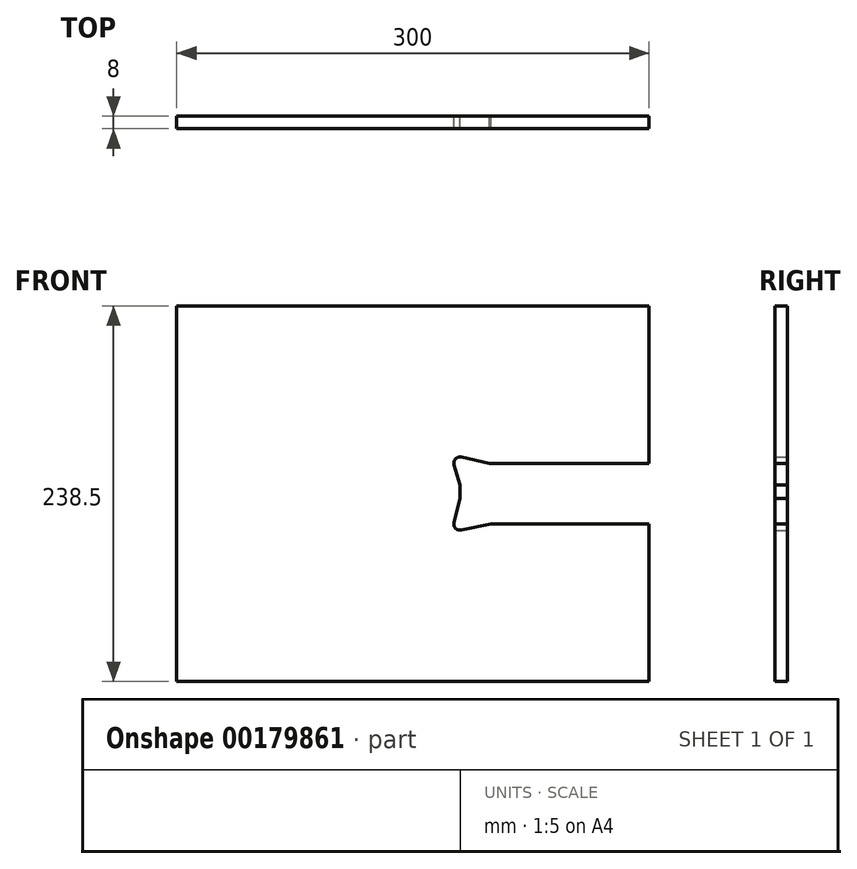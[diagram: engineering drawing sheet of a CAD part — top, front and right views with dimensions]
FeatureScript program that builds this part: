
annotation { "Feature Type Name" : "Feature", "Feature Type Description" : "" }
export const myFeature = defineFeature(function(context is Context, id is Id, definition is map)
    precondition{}
    {
        {
            var Q0;
            Q0=qCreatedBy(makeId("Front.planeOp"),FACE);
            var sketch = newSketch(context, id + "F0", { "sketchPlane" : qUnion([Q0])});
            skLineSegment(sketch, "E0", {"start": v(-40.97, 135.67) * mm, "end": v(79.03, 135.67) * mm});
            skLineSegment(sketch, "E1", {"start": v(79.03, 135.67) * mm, "end": v(79.03, 235.67) * mm});
            skLineSegment(sketch, "E2", {"start": v(79.03, 235.67) * mm, "end": v(-220.97, 235.67) * mm});
            skLineSegment(sketch, "E3", {"start": v(-40.97, 97.17) * mm, "end": v(-40.97, 135.67) * mm});
            skLineSegment(sketch, "E4", {"start": v(-40.97, 97.17) * mm, "end": v(79.03, 97.17) * mm});
            skLineSegment(sketch, "E5", {"start": v(79.03, 97.17) * mm, "end": v(79.03, -2.83) * mm});
            skLineSegment(sketch, "E6", {"start": v(79.03, -2.83) * mm, "end": v(-220.97, -2.83) * mm});
            skLineSegment(sketch, "E7", {"start": v(-220.97, -2.83) * mm, "end": v(-220.97, 235.67) * mm});
            skCircle(sketch, "E8", {"center": v(-40.97, 135.67) * mm, "radius": 4 * mm});
            skCircle(sketch, "E9", {"center": v(-40.97, 97.17) * mm, "radius": 4 * mm});
            skLineSegment(sketch, "E10", {"start": v(-40.11, 139.58) * mm, "end": v(-22.22, 135.67) * mm});
            skLineSegment(sketch, "E11", {"start": v(-44.8, 134.51) * mm, "end": v(-40.97, 121.87) * mm});
            skLineSegment(sketch, "E12", {"start": v(-44.84, 98.17) * mm, "end": v(-40.97, 113.2) * mm});
            skLineSegment(sketch, "E13", {"start": v(-40.15, 93.26) * mm, "end": v(-21.22, 97.17) * mm});
            skSolve(sketch);
        }
        {
            var Q0;
            {var subQ7=sQuery(id+"F0.wireOp",EDGE,"E1");Q0=makeQuery(id+"F0.imprint","IMPRINT",FACE,{"disambiguationData":[TD([[makeQuery(id+"F0.imprint","IMPRINT",EDGE,{"derivedFrom":subQ7}),1.0]])]});}
            extrude(context, id + "F1", {"entities" : qUnion([Q0]), "depth" : 8 * mm});
        }
    });
